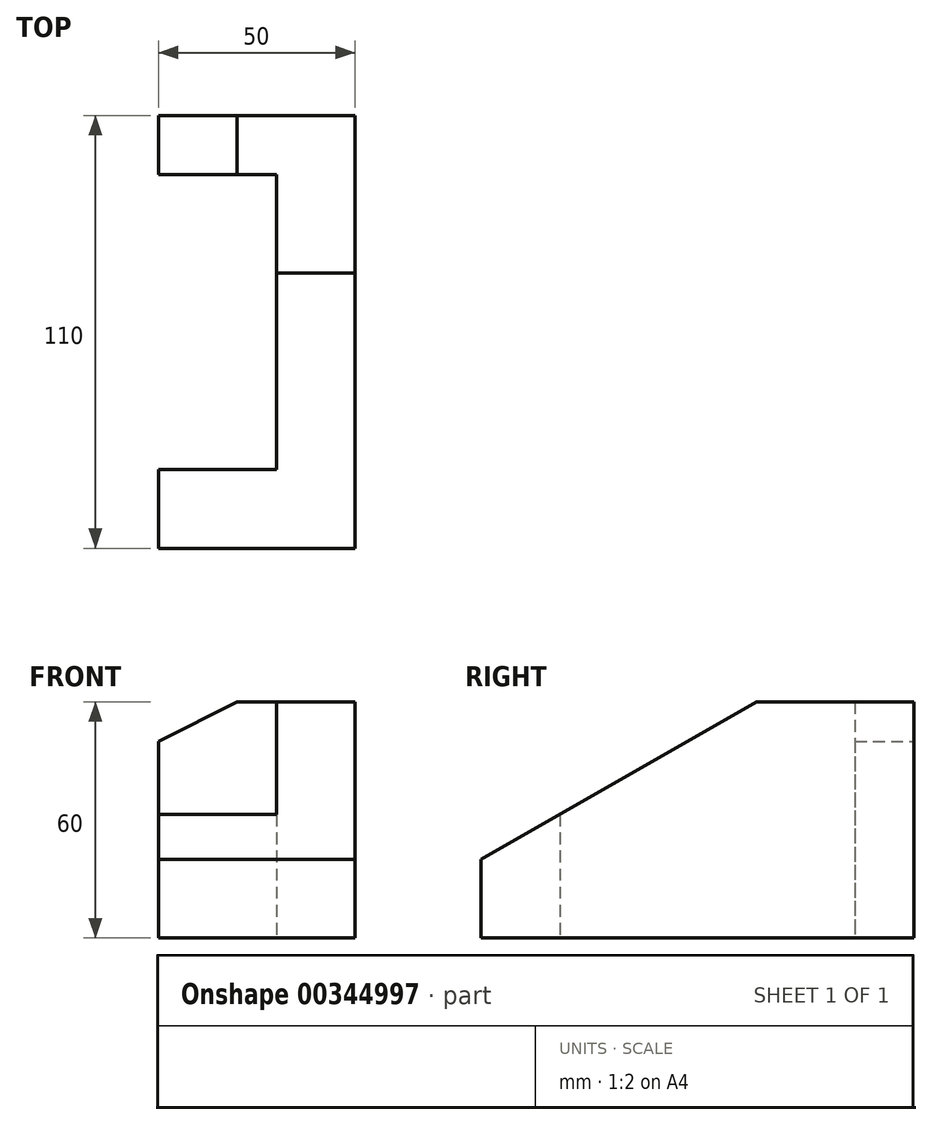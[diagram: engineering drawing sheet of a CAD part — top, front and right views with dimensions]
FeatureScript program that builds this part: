
annotation { "Feature Type Name" : "Feature", "Feature Type Description" : "" }
export const myFeature = defineFeature(function(context is Context, id is Id, definition is map)
    precondition{}
    {
        {
            var Q0;
            Q0=qCreatedBy(makeId("Top.planeOp"),FACE);
            var sketch = newSketch(context, id + "F0", { "sketchPlane" : qUnion([Q0])});
            skLineSegment(sketch, "E0.bottom", {"start": v(25, 55) * mm, "end": v(-25, 55) * mm});
            skLineSegment(sketch, "E0.top", {"start": v(25, -55) * mm, "end": v(-25, -55) * mm});
            skLineSegment(sketch, "E0.left", {"start": v(25, 55) * mm, "end": v(25, -55) * mm});
            skLineSegment(sketch, "E0.right", {"start": v(-25, 55) * mm, "end": v(-25, 40) * mm});
            skPoint(sketch, "E0.middle", {"position": v(0, 0) * mm});
            skPoint(sketch, "E1", {"position": v(25, 15) * mm});
            skPoint(sketch, "E2", {"position": v(-5, 55) * mm});
            skPoint(sketch, "E3", {"position": v(5, 55) * mm});
            skLineSegment(sketch, "E4", {"start": v(5, 40) * mm, "end": v(5, -35) * mm});
            skPoint(sketch, "E5", {"position": v(-25, 40) * mm});
            skLineSegment(sketch, "E6", {"start": v(-25, 40) * mm, "end": v(5, 40) * mm});
            skPoint(sketch, "E7", {"position": v(-25, -35) * mm});
            skLineSegment(sketch, "E8", {"start": v(-25, -35) * mm, "end": v(5, -35) * mm});
            skLineSegment(sketch, "E9.trimOffspring", {"start": v(-25, -35) * mm, "end": v(-25, -55) * mm});
            skSolve(sketch);
        }
        {
            var Q0;
            Q0=makeQuery(id+"F0.imprint","IMPRINT",FACE,{"disambiguationData":[TD([[makeQuery(id+"F0.imprint","IMPRINT",EDGE,{"derivedFrom":sQuery(id+"F0.wireOp",EDGE,"E0.bottom")}),1.0]])]});
            extrude(context, id + "F1", {"entities" : qUnion([Q0]), "depth" : 60 * mm});
        }
        {
            var Q0;
            Q0=makeQuery(id+"F1.opExtrude","SWEPT_FACE",FACE,{"disambiguationData":[OSD([sQuery(id+"F0.wireOp",EDGE,"E0.bottom")])]});
            var sketch = newSketch(context, id + "F2", { "sketchPlane" : qUnion([Q0])});
            skPoint(sketch, "E10", {"position": v(5, 60) * mm});
            skLineSegment(sketch, "E11", {"start": v(5, 60) * mm, "end": v(25, 50) * mm});
            skLineSegment(sketch, "E12.0", {"start": v(5, 60) * mm, "end": v(25, 60) * mm});
            skLineSegment(sketch, "E12.1", {"start": v(25, 60) * mm, "end": v(25, 50) * mm});
            skPoint(sketch, "E13.orphan", {"position": v(-25, 60) * mm});
            skPoint(sketch, "E14.orphan", {"position": v(25, 0) * mm});
            skSolve(sketch);
        }
        {
            var Q0;
            Q0=makeQuery(id+"F2.imprint","IMPRINT",FACE,{"disambiguationData":[TD([[makeQuery(id+"F2.imprint","IMPRINT",EDGE,{"derivedFrom":sQuery(id+"F2.wireOp",EDGE,"E11")}),1.0]])]});
            extrude(context, id + "F3", {"entities" : qUnion([Q0]), "operationType" : NewBodyOperationType.REMOVE, "oppositeDirection" : true, "depth" : 15 * mm});
        }
        {
            var Q0;
            Q0=makeQuery(id+"F1.opExtrude","SWEPT_FACE",FACE,{"disambiguationData":[OSD([sQuery(id+"F0.wireOp",EDGE,"E0.left")])]});
            var sketch = newSketch(context, id + "F4", { "sketchPlane" : qUnion([Q0])});
            skPoint(sketch, "E15", {"position": v(15, 60) * mm});
            skPoint(sketch, "E16", {"position": v(-55, 20) * mm});
            skLineSegment(sketch, "E17.0", {"start": v(15, 60) * mm, "end": v(-55, 60) * mm});
            skLineSegment(sketch, "E18.0", {"start": v(-55, 60) * mm, "end": v(-55, 20) * mm});
            skLineSegment(sketch, "E19", {"start": v(-55, 20) * mm, "end": v(15, 60) * mm});
            skPoint(sketch, "E20.orphan", {"position": v(55, 60) * mm});
            skPoint(sketch, "E21.orphan", {"position": v(-55, 0) * mm});
            skSolve(sketch);
        }
        {
            var Q0;
            Q0=makeQuery(id+"F4.imprint","IMPRINT",FACE,{"disambiguationData":[TD([[makeQuery(id+"F4.imprint","IMPRINT",EDGE,{"derivedFrom":sQuery(id+"F4.wireOp",EDGE,"E17.0")}),1.0]])]});
            extrude(context, id + "F5", {"entities" : qUnion([Q0]), "operationType" : NewBodyOperationType.REMOVE, "oppositeDirection" : true, "depth" : 50 * mm});
        }
    });
